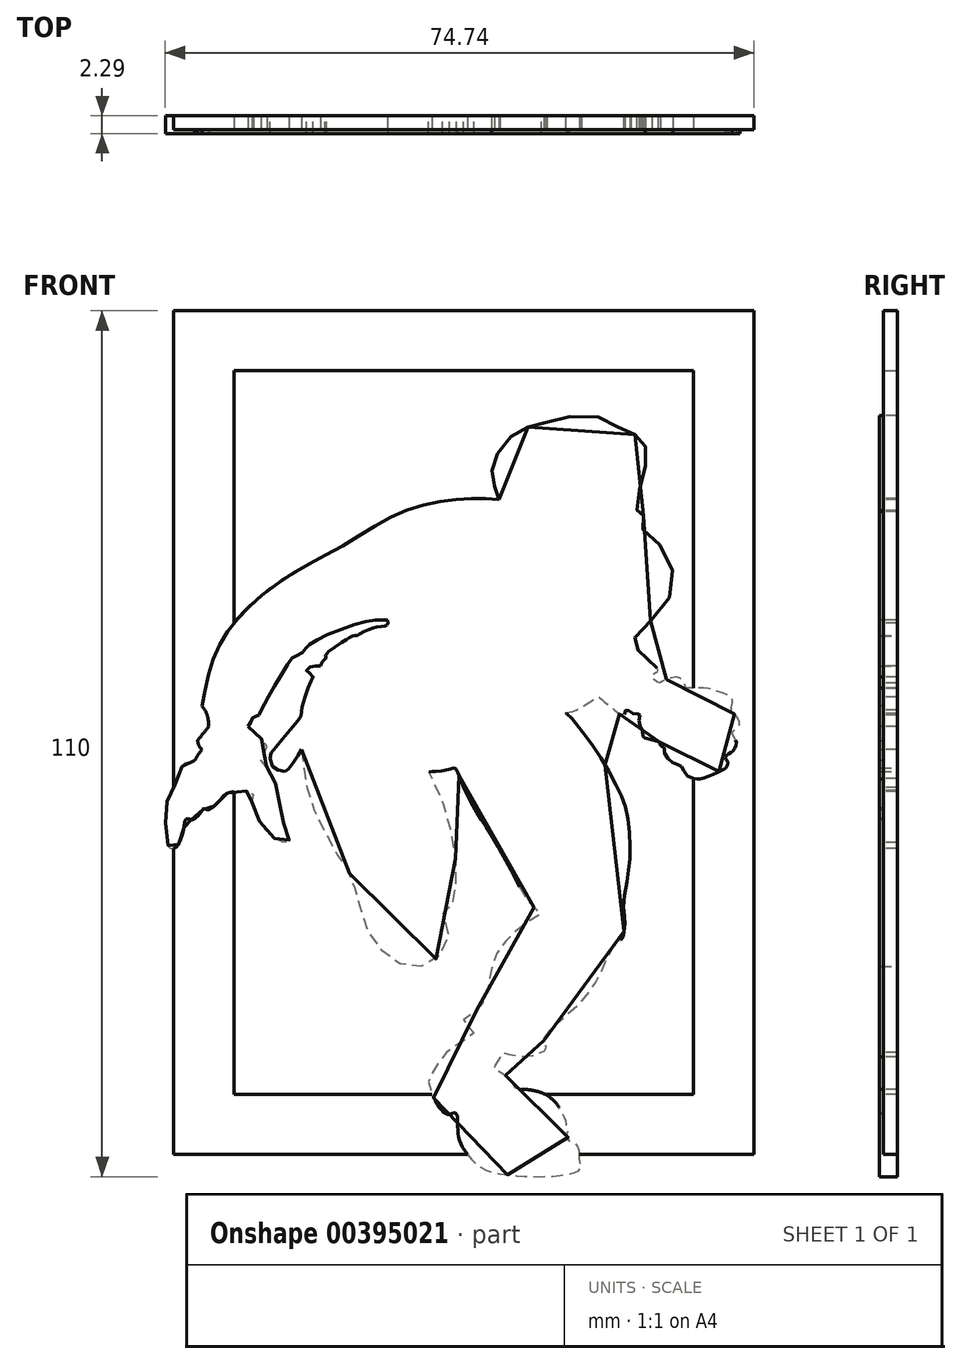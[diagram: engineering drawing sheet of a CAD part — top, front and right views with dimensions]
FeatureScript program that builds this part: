
annotation { "Feature Type Name" : "Feature", "Feature Type Description" : "" }
export const myFeature = defineFeature(function(context is Context, id is Id, definition is map)
    precondition{}
    {
        {
            var Q0;
            Q0=qCreatedBy(makeId("Front.planeOp"),FACE);
            var sketch = newSketch(context, id + "F0", { "sketchPlane" : qUnion([Q0])});
            skLineSegment(sketch, "E0", {"start": v(-44.45, 0) * mm, "end": v(44.45, 0) * mm, "construction": true});
            skLineSegment(sketch, "E1", {"start": v(0, 54.2) * mm, "end": v(0, -54.2) * mm, "construction": true});
            skPoint(sketch, "E2", {"position": v(0, 0) * mm});
            skFitSpline(sketch, "E3", {"points": [v(2.07, 37.23) * mm, v(-1.65, 37.35) * mm, v(-6.55, 36.74) * mm, v(-12, 34.82) * mm, v(-17.89, 31.29) * mm, v(-23.96, 27.94) * mm, v(-29.23, 24.04) * mm, v(-32.63, 20.14) * mm, v(-34.62, 15.8) * mm, v(-35.67, 10.97) * mm], "startDerivative": vector(-39.23, 2.67) * mm, "endDerivative": vector(-8.2, -46.44) * mm});
            skFitSpline(sketch, "E4", {"points": [v(-35.67, 10.97) * mm, v(-35.05, 9.98) * mm, v(-34.8, 8.37) * mm], "startDerivative": vector(1.56, -1.97) * mm, "endDerivative": vector(0.22, -3.2) * mm});
            skFitSpline(sketch, "E5", {"points": [v(-34.8, 8.37) * mm, v(-35.67, 7.32) * mm, v(-36.23, 6.57) * mm], "startDerivative": vector(-1.68, -2) * mm, "endDerivative": vector(-1.15, -1.58) * mm});
            skFitSpline(sketch, "E6", {"points": [v(-36.23, 6.57) * mm, v(-36.05, 5.96) * mm, v(-35.67, 5.44) * mm], "startDerivative": vector(0.24, -1.29) * mm, "endDerivative": vector(0.87, -1) * mm});
            skFitSpline(sketch, "E7", {"points": [v(-35.67, 5.44) * mm, v(-36.23, 4.68) * mm, v(-36.6, 4.04) * mm], "startDerivative": vector(-1.12, -1.44) * mm, "endDerivative": vector(-0.72, -1.34) * mm});
            skFitSpline(sketch, "E8", {"points": [v(-36.6, 4.04) * mm, v(-37.4, 3.8) * mm, v(-38.03, 3.54) * mm, v(-38.84, 1.98) * mm, v(-39.13, 0.94) * mm, v(-39.88, -0.55) * mm, v(-40.22, -1.48) * mm, v(-40.32, -3.46) * mm, v(-40.17, -5.86) * mm, v(-39.72, -7.06) * mm, v(-39.1, -7.06) * mm, v(-38.63, -6.6) * mm, v(-38.08, -4.98) * mm, v(-37.95, -4.27) * mm, v(-37.67, -3.33) * mm, v(-37.15, -3.44) * mm, v(-36.6, -3.34) * mm, v(-35.66, -2.35) * mm, v(-35.43, -1.98) * mm, v(-35, -2.19) * mm, v(-33.73, -1.33) * mm, v(-32.77, -0.24) * mm, v(-32.14, 0) * mm, v(-30.6, 0.26) * mm, v(-29.17, -0.21) * mm, v(-29.25, -0.81) * mm, v(-29.15, -1.98) * mm, v(-28.34, -3.68) * mm, v(-27.12, -5.27) * mm, v(-25.47, -6.28) * mm, v(-24.61, -6.2) * mm, v(-24.77, -5.58) * mm, v(-25.21, -4.22) * mm, v(-25.63, -2.71) * mm, v(-25.94, -0.47) * mm, v(-26.1, 0.6) * mm, v(-26.67, 2.03) * mm, v(-27.4, 3.2) * mm, v(-28.13, 4.04) * mm, v(-27.9, 4.79) * mm, v(-27.43, 5.73) * mm, v(-27.95, 6.64) * mm, v(-29.36, 8.02) * mm, v(-29.82, 8.36) * mm], "startDerivative": vector(-42.25, -13.95) * mm, "endDerivative": vector(-24.4, 15.47) * mm});
            skFitSpline(sketch, "E9", {"points": [v(-29.82, 8.36) * mm, v(-29.54, 8.76) * mm, v(-29.29, 9.4) * mm, v(-29.21, 9.55) * mm, v(-28.84, 9.64) * mm, v(-28.49, 9.78) * mm, v(-28.35, 9.97) * mm, v(-27.95, 10.85) * mm, v(-27.23, 12.18) * mm, v(-25.33, 15.4) * mm, v(-24.23, 17.07) * mm, v(-23.95, 17.26) * mm, v(-22.92, 17.77) * mm, v(-22.57, 18.23) * mm, v(-22.13, 18.67) * mm, v(-20.6, 19.63) * mm, v(-16.42, 21.28) * mm, v(-13.78, 21.93) * mm, v(-12.5, 21.91) * mm, v(-12.08, 21.88) * mm], "startDerivative": vector(8.09, 9.48) * mm, "endDerivative": vector(10.9, -0.8) * mm});
            skFitSpline(sketch, "E10", {"points": [v(-12.08, 21.88) * mm, v(-12.08, 21.42) * mm, v(-12.23, 21.22) * mm, v(-12.42, 21.16) * mm, v(-13.52, 21.03) * mm, v(-14.4, 20.72) * mm, v(-15.7, 20.12) * mm, v(-15.98, 19.92) * mm, v(-16.34, 19.95) * mm, v(-16.88, 19.73) * mm, v(-17.73, 19.19) * mm, v(-19.98, 17.47) * mm, v(-19.96, 17.24) * mm, v(-19.87, 17.15) * mm, v(-20.35, 16.62) * mm, v(-20.6, 16.12) * mm, v(-20.63, 16.05) * mm], "startDerivative": vector(1.15, -9.1) * mm, "endDerivative": vector(-1.16, -2.5) * mm});
            skFitSpline(sketch, "E11", {"points": [v(-20.63, 16.05) * mm, v(-20.99, 16.05) * mm, v(-21.48, 16.05) * mm, v(-22.06, 15.87) * mm, v(-22.4, 15.52) * mm, v(-22.39, 15.48) * mm, v(-22.29, 15.37) * mm, v(-21.85, 15.03) * mm, v(-21.56, 14.7) * mm, v(-21.68, 14.47) * mm, v(-21.92, 13.92) * mm, v(-22.39, 12.77) * mm, v(-22.93, 10.92) * mm, v(-23.13, 9.6) * mm, v(-23.22, 9.4) * mm, v(-24.7, 7.74) * mm, v(-25.96, 6.1) * mm, v(-26.86, 5.07) * mm, v(-26.94, 4.79) * mm, v(-26.97, 3.78) * mm, v(-26.3, 2.95) * mm, v(-25.67, 2.77) * mm, v(-24.86, 2.73) * mm, v(-24.73, 2.93) * mm, v(-24.23, 3.58) * mm, v(-23.42, 4.79) * mm, v(-23.02, 5.44) * mm], "startDerivative": vector(-12.7, -0.16) * mm, "endDerivative": vector(8.85, 14.94) * mm});
            skFitSpline(sketch, "E12", {"points": [v(-23.02, 5.44) * mm, v(-22.87, 4.04) * mm, v(-22.52, 1.55) * mm, v(-22.23, 0.32) * mm, v(-21.34, -2.46) * mm, v(-20.22, -4.7) * mm, v(-18.43, -7.97) * mm, v(-17.5, -9.26) * mm, v(-17.11, -9.85) * mm, v(-16.35, -11.96) * mm, v(-15.51, -14.7) * mm, v(-15.02, -16.76) * mm, v(-13.69, -19.06) * mm, v(-11.74, -21) * mm, v(-9.6, -21.97) * mm, v(-7.28, -21.9) * mm, v(-5.42, -20.6) * mm, v(-4.4, -18.72) * mm, v(-4.3, -17.26) * mm, v(-4.49, -16.98) * mm, v(-5.08, -15.84) * mm, v(-5.1, -15.53) * mm, v(-4.98, -15.28) * mm, v(-4.43, -15) * mm, v(-3.9, -14.23) * mm, v(-3.5, -12.93) * mm, v(-3.37, -10.33) * mm, v(-3.62, -6.89) * mm, v(-4.58, -2.83) * mm, v(-5.54, 0) * mm, v(-6.6, 1.91) * mm, v(-6.9, 2.5) * mm, v(-6.72, 2.65) * mm, v(-6.28, 2.65) * mm, v(-4.92, 2.78) * mm, v(-3.53, 3.12) * mm, v(-3.34, 2.93) * mm, v(-2.75, 1.48) * mm, v(-1.73, -0.82) * mm, v(-0.34, -3.2) * mm, v(1.34, -5.8) * mm, v(2.4, -7.73) * mm, v(4.47, -11.54) * mm, v(5.52, -13.49) * mm, v(6.8, -14.85) * mm, v(7.4, -15.4) * mm, v(7.4, -15.5) * mm, v(7.13, -15.6) * mm, v(5.02, -16.96) * mm, v(2.98, -18.78) * mm, v(1.46, -21.14) * mm, v(0.84, -23.86) * mm, v(0.35, -25.81) * mm, v(-0.7, -27.64) * mm, v(-2.41, -28.82) * mm, v(-2.07, -29.56) * mm, v(-1.11, -30.43) * mm, v(-1.2, -30.57) * mm, v(-1.94, -31.22) * mm, v(-3.87, -32.43) * mm, v(-5.38, -33.96) * mm, v(-6.52, -35.76) * mm, v(-6.9, -36.8) * mm, v(-6.02, -39.24) * mm, v(-4.99, -40.62) * mm, v(-4.35, -40.88) * mm, v(-3.72, -40.7) * mm, v(-3.39, -40.77) * mm, v(-3.2, -41.58) * mm, v(-3.15, -43.24) * mm, v(-2.63, -44.95) * mm, v(-1, -47.03) * mm, v(1.04, -48.18) * mm, v(5.04, -48.73) * mm, v(8.1, -48.78) * mm, v(11.42, -48.36) * mm, v(12.5, -47.63) * mm, v(12.47, -47.23) * mm, v(12.4, -47.21) * mm, v(12.32, -46.87) * mm, v(12.29, -45.97) * mm, v(12.03, -44.86) * mm, v(11.4, -44.38) * mm, v(10.93, -44.3) * mm, v(10.93, -44.18) * mm, v(10.74, -43.59) * mm, v(10.63, -43.43) * mm, v(10.8, -43.16) * mm, v(10.7, -42.78) * mm, v(10.62, -42) * mm, v(10, -40.5) * mm, v(8.68, -38.82) * mm, v(7.33, -38.1) * mm, v(5.52, -37.72) * mm, v(4.39, -37.7) * mm, v(4.17, -37.56) * mm, v(3.6, -36.65) * mm, v(2.53, -35.73) * mm, v(1.52, -35.15) * mm, v(1.57, -34.96) * mm, v(1.6, -34.73) * mm, v(2.23, -33.66) * mm, v(2.51, -33.07) * mm, v(2.6, -33.02) * mm, v(3.07, -33.16) * mm, v(4.73, -33.55) * mm, v(6.94, -33.26) * mm, v(8.1, -32.55) * mm, v(8.15, -32.4) * mm, v(8.01, -32.22) * mm, v(7.77, -32.1) * mm, v(7.77, -31.88) * mm, v(7.81, -31.26) * mm, v(9.05, -29.65) * mm, v(12.12, -26.97) * mm, v(14.04, -24.59) * mm, v(15.37, -22.05) * mm, v(16.32, -19.96) * mm, v(17.5, -18.75) * mm, v(17.87, -18.33) * mm, v(17.9, -17.85) * mm, v(18.05, -16.41) * mm, v(17.87, -14.7) * mm, v(18.4, -10.76) * mm, v(18.7, -7.41) * mm, v(18.3, -2.7) * mm, v(17.15, 0.53) * mm, v(14.3, 5.44) * mm, v(12.15, 8.36) * mm, v(10.66, 10.01) * mm, v(10.5, 10.1) * mm, v(10.6, 10.12) * mm, v(11.72, 10.45) * mm, v(14.2, 11.89) * mm, v(14.72, 12.15) * mm, v(14.84, 12.06) * mm, v(16.15, 10.99) * mm, v(17.32, 10.01) * mm, v(17.56, 9.97) * mm, v(17.76, 10.01) * mm, v(17.91, 9.86) * mm, v(18.05, 9.97) * mm, v(18.11, 10.4) * mm, v(18.25, 10.5) * mm, v(18.67, 10.27) * mm, v(19.2, 9.96) * mm, v(19.83, 10.01) * mm, v(19.97, 9.98) * mm, v(19.86, 9.65) * mm, v(19.91, 8.7) * mm, v(19.99, 8.36) * mm, v(20.42, 7.44) * mm, v(20.33, 7.02) * mm, v(20.48, 6.96) * mm, v(21.74, 6.64) * mm, v(22.54, 6.34) * mm, v(22.56, 6.17) * mm, v(22.57, 5.9) * mm, v(22.73, 5.86) * mm, v(22.98, 5.73) * mm, v(23.06, 5.6) * mm, v(23.09, 5.1) * mm, v(23.5, 4.31) * mm, v(24.15, 3.78) * mm, v(24.76, 3.55) * mm, v(25.2, 3.33) * mm, v(25.49, 2.87) * mm, v(25.97, 2.14) * mm, v(27, 1.72) * mm, v(28.18, 1.9) * mm, v(30.32, 2.8) * mm, v(30.88, 3.13) * mm, v(30.97, 3.28) * mm, v(31.1, 3.63) * mm, v(31.02, 4.04) * mm, v(30.82, 4.43) * mm, v(31.06, 4.79) * mm, v(31.73, 5.25) * mm, v(32.2, 6.06) * mm, v(32.06, 6.77) * mm, v(31.71, 7.44) * mm, v(31.73, 7.7) * mm, v(32.21, 8.15) * mm, v(32.61, 8.49) * mm, v(32.54, 9.19) * mm, v(32.09, 9.88) * mm, v(31.58, 10.38) * mm, v(31.67, 11.1) * mm, v(31.7, 11.77) * mm, v(31.44, 12.2) * mm, v(29.89, 12.81) * mm, v(28.45, 13.25) * mm, v(27.2, 13.3) * mm, v(26.03, 13.26) * mm, v(25.84, 13.26) * mm, v(25.56, 13.91) * mm, v(24.71, 14.67) * mm, v(23.97, 14.55) * mm, v(22.93, 14.22) * mm, v(22.33, 13.94) * mm, v(21.46, 14.77) * mm, v(21.5, 14.89) * mm, v(21.9, 15.2) * mm, v(22.23, 15.4) * mm, v(22.1, 15.8) * mm, v(21.58, 16.3) * mm, v(19.35, 18.5) * mm, v(18.86, 19.24) * mm, v(18.9, 19.41) * mm, v(19.4, 19.8) * mm, v(20.08, 20.7) * mm, v(22.02, 22.45) * mm, v(23.58, 24.5) * mm, v(24.15, 26.66) * mm, v(23.9, 28.92) * mm, v(22.75, 31.14) * mm, v(21.37, 32.51) * mm, v(20.38, 33.38) * mm, v(20.25, 33.57) * mm, v(20.27, 33.97) * mm, v(20.4, 35) * mm, v(20.34, 35.5) * mm, v(19.9, 35.84) * mm, v(19.52, 35.67) * mm, v(19.6, 35.95) * mm, v(19.7, 36.93) * mm, v(19.9, 38.35) * mm, v(20.44, 40.07) * mm, v(20.65, 42.1) * mm, v(20.6, 43.42) * mm, v(20.65, 43.96) * mm, v(20.3, 44.36) * mm, v(19.66, 45.28) * mm, v(19.2, 45.5) * mm, v(17.7, 46.18) * mm, v(17.26, 46.36) * mm, v(16.64, 46.89) * mm, v(15.15, 47.59) * mm, v(13, 47.88) * mm, v(10.41, 47.7) * mm, v(8.6, 47.25) * mm, v(7.2, 46.72) * mm, v(6.45, 46.52) * mm, v(5.4, 46.36) * mm, v(4.39, 45.8) * mm, v(3.55, 45.17) * mm, v(2.96, 44.46) * mm, v(1.79, 42.94) * mm, v(1.23, 41.9) * mm, v(1.17, 41.04) * mm, v(1.14, 40.47) * mm, v(1.26, 39.72) * mm, v(1.5, 38.93) * mm, v(1.9, 38.14) * mm, v(2.2, 37.37) * mm, v(2.07, 37.23) * mm], "startDerivative": vector(28.4, -278.9) * mm, "endDerivative": vector(-112.4, -58) * mm});
            skSolve(sketch);
        }
        {
            var Q0;
            Q0=qSketchRegion(id+"F0",true);
            extrude(context, id + "F1", {"entities" : qUnion([Q0]), "oppositeDirection" : true, "depth" : 2.3 * mm});
        }
        {
            var Q0;
            Q0=makeQuery(id+"F1.opExtrude","CAP_FACE",FACE,{"disambiguationData":[OSD([sQuery(id+"F0.wireOp",EDGE,"E3"),sQuery(id+"F0.wireOp",EDGE,"E4"),sQuery(id+"F0.wireOp",EDGE,"E5"),sQuery(id+"F0.wireOp",EDGE,"E6"),sQuery(id+"F0.wireOp",EDGE,"E7"),sQuery(id+"F0.wireOp",EDGE,"E8"),sQuery(id+"F0.wireOp",EDGE,"E9"),sQuery(id+"F0.wireOp",EDGE,"E10"),sQuery(id+"F0.wireOp",EDGE,"E11"),sQuery(id+"F0.wireOp",EDGE,"E12")])],"isStart":true});
            var sketch = newSketch(context, id + "F2", { "sketchPlane" : qUnion([Q0])});
            skFitSpline(sketch, "E13", {"points": [v(2.3, 37.05) * mm, v(2.58, 36.42) * mm, v(3.02, 35.55) * mm, v(3.78, 34.43) * mm, v(4.11, 33.95) * mm, v(3.9, 34.93) * mm, v(3.78, 36.33) * mm, v(3.76, 37.93) * mm, v(4.08, 40.22) * mm, v(5.22, 41.8) * mm, v(6.51, 42.35) * mm, v(8.55, 42.6) * mm, v(10.3, 41.98) * mm, v(12.03, 41.25) * mm, v(13.24, 41.14) * mm, v(15.06, 42.24) * mm, v(15.9, 42.8) * mm, v(17.03, 42.87) * mm, v(18.19, 42) * mm, v(18.91, 40.62) * mm, v(19.02, 39.55) * mm, v(19.04, 37.2) * mm, v(18.95, 34.57) * mm, v(19, 33.73) * mm, v(19.07, 34.15) * mm, v(19.36, 35.43) * mm], "startDerivative": vector(9.4, -21.56) * mm, "endDerivative": vector(8.5, 34.59) * mm});
            skFitSpline(sketch, "E14", {"points": [v(2.1, 34.71) * mm, v(2.62, 34.14) * mm, v(3, 33.38) * mm, v(3.32, 32.65) * mm], "startDerivative": vector(1.66, -1.65) * mm, "endDerivative": vector(0.92, -2.17) * mm});
            skFitSpline(sketch, "E15", {"points": [v(2.75, 35.87) * mm, v(2.36, 36.1) * mm, v(1.85, 36.13) * mm, v(1.42, 35.5) * mm, v(1.33, 34.5) * mm, v(1.77, 32.8) * mm, v(2.16, 31.91) * mm], "startDerivative": vector(-3.01, 1.98) * mm, "endDerivative": vector(2.16, -4.4) * mm});
            skFitSpline(sketch, "E16", {"points": [v(20.12, 33.4) * mm, v(19.68, 32.59) * mm, v(19.1, 31.64) * mm], "startDerivative": vector(-0.86, -1.7) * mm, "endDerivative": vector(-1.15, -1.84) * mm});
            skFitSpline(sketch, "E17", {"points": [v(18.98, 33.52) * mm, v(19.02, 31.13) * mm, v(19, 29) * mm, v(18.85, 28.03) * mm, v(17.83, 25.6) * mm, v(16.9, 24.46) * mm, v(16.28, 23.96) * mm, v(15.73, 23.27) * mm, v(13.64, 22.24) * mm, v(10.64, 22.21) * mm, v(8.36, 23.27) * mm, v(7.22, 24.24) * mm, v(6.02, 25.1) * mm, v(5.06, 26.35) * mm, v(4.5, 27.73) * mm, v(4.37, 28.62) * mm, v(4.01, 29.65) * mm], "startDerivative": vector(0.48, -30.88) * mm, "endDerivative": vector(-8.43, 20.55) * mm});
            skCircle(sketch, "E18", {"center": v(2.83, 30.82) * mm, "radius": 1.11 * mm});
            skFitSpline(sketch, "E19", {"points": [v(11.33, 29.52) * mm, v(12.1, 29.5) * mm, v(12.71, 29.21) * mm, v(13.35, 29) * mm, v(14.18, 29.32) * mm, v(15, 29.8) * mm, v(15.54, 29.87) * mm], "startDerivative": vector(4.72, 0.3) * mm, "endDerivative": vector(3.72, -0.03) * mm});
            skFitSpline(sketch, "E20", {"points": [v(8, 27.33) * mm, v(7.78, 26.98) * mm, v(7.76, 26.5) * mm, v(7.94, 26.32) * mm], "startDerivative": vector(-0.72, -0.88) * mm, "endDerivative": vector(0.77, -0.49) * mm});
            skFitSpline(sketch, "E21", {"points": [v(9.51, 26.98) * mm, v(10.68, 27.5) * mm, v(11.66, 27.88) * mm, v(13.1, 27.88) * mm, v(13.76, 27.84) * mm, v(14.7, 28.12) * mm, v(15.67, 28.01) * mm, v(16.44, 27.46) * mm], "startDerivative": vector(7.64, 3.36) * mm, "endDerivative": vector(5.28, -4.62) * mm});
            skFitSpline(sketch, "E22", {"points": [v(17.64, 27.4) * mm, v(17.36, 27.6) * mm, v(17.03, 27.64) * mm, v(16.61, 27.35) * mm, v(16.13, 27.07) * mm, v(14.84, 26.65) * mm, v(13.87, 26.2) * mm, v(13.52, 25.93) * mm, v(13.22, 25.9) * mm, v(12.54, 26.13) * mm, v(11.49, 26.46) * mm, v(10.68, 26.5) * mm, v(9.51, 26.46) * mm, v(9.01, 26.48) * mm, v(8.84, 26.65) * mm], "startDerivative": vector(-5.14, 4.15) * mm, "endDerivative": vector(-3.27, 4.66) * mm});
            skFitSpline(sketch, "E23", {"points": [v(9.8, 25.5) * mm, v(10.48, 24.86) * mm, v(11.55, 24.09) * mm, v(12.73, 23.98) * mm, v(14.55, 24.44) * mm, v(15.34, 25.18) * mm, v(15.65, 25.73) * mm, v(15.73, 26.24) * mm], "startDerivative": vector(4.64, -4.44) * mm, "endDerivative": vector(0.49, 5.08) * mm});
            skFitSpline(sketch, "E24", {"points": [v(7.18, 35.08) * mm, v(8.25, 35.2) * mm, v(9.68, 34.96) * mm, v(10.6, 34.45) * mm, v(11.1, 34.03) * mm, v(11.78, 34.17) * mm, v(12.24, 34.85) * mm], "startDerivative": vector(5.68, 1.09) * mm, "endDerivative": vector(2.35, 5) * mm});
            skFitSpline(sketch, "E25", {"points": [v(8.43, 36.51) * mm, v(9.37, 36.5) * mm, v(9.88, 36.07) * mm, v(10.6, 35.3) * mm, v(11.06, 34.32) * mm], "startDerivative": vector(4.14, 0.43) * mm, "endDerivative": vector(1.4, -3.78) * mm});
            skFitSpline(sketch, "E26", {"points": [v(7.45, 34.93) * mm, v(7.79, 34.48) * mm, v(8.1, 34.15) * mm, v(8.5, 33.81) * mm], "startDerivative": vector(0.99, -1.35) * mm, "endDerivative": vector(1.29, -1) * mm});
            skFitSpline(sketch, "E27", {"points": [v(9.2, 34.93) * mm, v(9.17, 34.51) * mm, v(9.3, 34.06) * mm, v(9.63, 33.96) * mm, v(9.99, 34.07) * mm, v(10.2, 34.38) * mm, v(10.26, 34.6) * mm], "startDerivative": vector(-0.42, -2.2) * mm, "endDerivative": vector(0.26, 1.57) * mm});
            skFitSpline(sketch, "E28", {"points": [v(14.93, 34.15) * mm, v(15.66, 35) * mm, v(16.27, 35.94) * mm, v(16.71, 36.89) * mm], "startDerivative": vector(2.23, 2.47) * mm, "endDerivative": vector(1.24, 2.95) * mm});
            skFitSpline(sketch, "E29", {"points": [v(15.66, 34.68) * mm, v(15.81, 34.22) * mm, v(16.1, 33.98) * mm, v(16.46, 34.14) * mm, v(16.66, 34.56) * mm, v(16.67, 35.15) * mm], "startDerivative": vector(0.53, -2.35) * mm, "endDerivative": vector(-0.14, 2.7) * mm});
            skFitSpline(sketch, "E30", {"points": [v(16, 35.21) * mm, v(16.55, 35.33) * mm, v(17.23, 35.29) * mm, v(17.78, 35.41) * mm, v(18.39, 35.82) * mm], "startDerivative": vector(2.2, 0.72) * mm, "endDerivative": vector(2.24, 1.73) * mm});
            skFitSpline(sketch, "E31", {"points": [v(17.64, 35.26) * mm, v(17.6, 34.85) * mm, v(17.35, 34.48) * mm, v(17.05, 34.12) * mm], "startDerivative": vector(0.02, -1.3) * mm, "endDerivative": vector(-0.85, -1.05) * mm});
            skFitSpline(sketch, "E32", {"points": [v(2.55, 38.25) * mm, v(2.17, 41.02) * mm, v(2.94, 42.4) * mm, v(4.56, 43.73) * mm, v(5.23, 43.95) * mm, v(4.02, 44.05) * mm, v(4.88, 44.67) * mm, v(7.66, 45.86) * mm], "startDerivative": vector(-4.09, 16.61) * mm, "endDerivative": vector(14.9, 6.03) * mm});
            skSolve(sketch);
        }
        {
            var Q0;
            Q0=qSketchRegion(id+"F2",true);
            var Q1;
            Q1=sQuery(id+"F2.wireOp",EDGE,"d9569821-eecf-49fa-9423-2ff2d1b1941c");
            var Q2;
            Q2=sQuery(id+"F2.wireOp",EDGE,"7pOSf9LI-wKQY-qpFU-wMJt-ItYx99x1vwxx");
            var Q3;
            Q3=sQuery(id+"F2.wireOp",EDGE,"vgNLgwYX-bfzJ-7AqC-6rUm-0AJOgbjPAZjm");
            var Q4;
            Q4=sQuery(id+"F2.wireOp",EDGE,"1a1bac1e-a555-4706-be7b-ffc530e547ce");
            var Q5;
            Q5=sQuery(id+"F2.wireOp",EDGE,"E13");
            var Q6;
            Q6=sQuery(id+"F2.wireOp",EDGE,"E16");
            var Q7;
            Q7=sQuery(id+"F2.wireOp",EDGE,"E17");
            var Q8;
            Q8=sQuery(id+"F2.wireOp",EDGE,"E18");
            var Q9;
            Q9=sQuery(id+"F2.wireOp",EDGE,"E15");
            var Q10;
            Q10=sQuery(id+"F2.wireOp",EDGE,"E14");
            var Q11;
            Q11=sQuery(id+"F2.wireOp",EDGE,"E19");
            var Q12;
            Q12=sQuery(id+"F2.wireOp",EDGE,"E21");
            var Q13;
            Q13=sQuery(id+"F2.wireOp",EDGE,"E20");
            var Q14;
            Q14=sQuery(id+"F2.wireOp",EDGE,"E23");
            var Q15;
            Q15=sQuery(id+"F2.wireOp",EDGE,"E22");
            var Q16;
            Q16=sQuery(id+"F2.wireOp",EDGE,"E26");
            var Q17;
            Q17=sQuery(id+"F2.wireOp",EDGE,"E24");
            var Q18;
            Q18=sQuery(id+"F2.wireOp",EDGE,"E27");
            var Q19;
            Q19=sQuery(id+"F2.wireOp",EDGE,"E25");
            var Q20;
            Q20=sQuery(id+"F2.wireOp",EDGE,"E28");
            var Q21;
            Q21=sQuery(id+"F2.wireOp",EDGE,"E29");
            var Q22;
            Q22=sQuery(id+"F2.wireOp",EDGE,"E30");
            var Q23;
            Q23=sQuery(id+"F2.wireOp",EDGE,"E31");
            var Q24;
            Q24=sQuery(id+"F2.wireOp",EDGE,"1e27200c-010a-4161-a363-a86046994168");
            var Q25;
            Q25=sQuery(id+"F2.wireOp",EDGE,"E32");
            extrude(context, id + "F3", {"entities" : qUnion([Q0]), "bodyType" : ToolBodyType.SURFACE, "surfaceEntities" : qUnion([Q1, Q2, Q3, Q4, Q5, Q6, Q7, Q8, Q9, Q10, Q11, Q12, Q13, Q14, Q15, Q16, Q17, Q18, Q19, Q20, Q21, Q22, Q23, Q24, Q25]), "depth" : 0.13 * mm});
        }
        {
            var Q0;
            Q0=makeQuery(id+"F0.imprint","IMPRINT",FACE,{"disambiguationData":[TD([[makeQuery(id+"F0.imprint","IMPRINT",EDGE,{"derivedFrom":sQuery(id+"F0.wireOp",EDGE,"E3")}),1.0]])]});
            var sketch = newSketch(context, id + "F4", { "sketchPlane" : qUnion([Q0])});
            skFitSpline(sketch, "E33", {"points": [v(-34.82, 10.54) * mm, v(-33.64, 11.76) * mm, v(-31.38, 12.43) * mm, v(-29.38, 10.8) * mm, v(-29.08, 9.98) * mm], "startDerivative": vector(4.16, 5.18) * mm, "endDerivative": vector(0.82, -4.17) * mm});
            skFitSpline(sketch, "E34", {"points": [v(-34.6, 8.06) * mm, v(-33.41, 8.58) * mm, v(-31.52, 8.72) * mm, v(-30.2, 8.4) * mm], "startDerivative": vector(3.49, 1.9) * mm, "endDerivative": vector(3.9, -1.32) * mm});
            skFitSpline(sketch, "E35", {"points": [v(-38.27, -3.9) * mm, v(-38.56, -4.35) * mm, v(-38.82, -4.43) * mm, v(-39.12, -3.32) * mm, v(-39.05, -0.54) * mm, v(-38.9, 0.54) * mm], "startDerivative": vector(-1.85, -3.5) * mm, "endDerivative": vector(0.74, 4.42) * mm});
            skFitSpline(sketch, "E36", {"points": [v(-36.71, 3.5) * mm, v(-37.23, 1.39) * mm, v(-37.71, -1.2) * mm, v(-37.75, -2.58) * mm, v(-37.53, -3.06) * mm], "startDerivative": vector(-1.76, -6.84) * mm, "endDerivative": vector(1.81, -2.9) * mm});
            skFitSpline(sketch, "E37", {"points": [v(-35.27, 5.61) * mm, v(-34.45, 5.8) * mm, v(-33.55, 5.48) * mm], "startDerivative": vector(1.67, 0.63) * mm, "endDerivative": vector(1.76, -0.88) * mm});
            skFitSpline(sketch, "E38", {"points": [v(-32.49, 0.54) * mm, v(-31.45, 2.06) * mm, v(-30.57, 3.39) * mm], "startDerivative": vector(2.05, 2.98) * mm, "endDerivative": vector(1.78, 2.72) * mm});
            skFitSpline(sketch, "E39", {"points": [v(-11.38, 22.24) * mm, v(-8.94, 22.87) * mm, v(-5.3, 23.79) * mm], "startDerivative": vector(5.14, 1.34) * mm, "endDerivative": vector(6.95, 1.74) * mm});
            skFitSpline(sketch, "E40", {"points": [v(-9.47, 22.42) * mm, v(-6.72, 22.27) * mm], "startDerivative": vector(2.75, -0.16) * mm, "endDerivative": vector(2.75, -0.16) * mm});
            skFitSpline(sketch, "E41", {"points": [v(-8.55, 23.34) * mm, v(-7.71, 25.18) * mm, v(-7.3, 28.27) * mm, v(-7.4, 30.91) * mm, v(-8.05, 33.24) * mm, v(-8.92, 34.84) * mm], "startDerivative": vector(5.1, 9.05) * mm, "endDerivative": vector(-5.22, 8.58) * mm});
            skFitSpline(sketch, "E42", {"points": [v(-12.06, 21.1) * mm, v(-12.09, 18.69) * mm, v(-11.44, 15.88) * mm, v(-10.6, 12.98) * mm, v(-10.12, 12.35) * mm, v(-8.6, 10.22) * mm, v(-7.19, 8.89) * mm, v(-6.7, 8.56) * mm, v(-6.45, 8.59) * mm, v(-5.2, 9.56) * mm, v(-3.14, 10.36) * mm, v(-0.44, 12.11) * mm, v(1.93, 14.5) * mm, v(3.32, 17.23) * mm, v(4.17, 20.44) * mm, v(4.05, 20.61) * mm, v(3.17, 21.15) * mm, v(1.59, 23.04) * mm, v(0.66, 25.07) * mm, v(-0.5, 27.74) * mm, v(-1.08, 30.66) * mm, v(-0.87, 33.24) * mm, v(0.78, 37.02) * mm], "startDerivative": vector(-3.53, -49.44) * mm, "endDerivative": vector(31.25, 61.75) * mm});
            skFitSpline(sketch, "E43", {"points": [v(-4.72, 19.77) * mm, v(-3.58, 19.4) * mm, v(-2.8, 19.09) * mm, v(-2.8, 19) * mm, v(-3.32, 18.26) * mm, v(-4.54, 16.65) * mm, v(-4.4, 16.64) * mm, v(-3.84, 16.57) * mm, v(-2.53, 16.5) * mm, v(-2.43, 16.6) * mm, v(-1.68, 17.82) * mm, v(-1.01, 18.8) * mm, v(-0.87, 18.8) * mm, v(-0.23, 18.72) * mm, v(0.78, 18.54) * mm, v(0.91, 18.58) * mm, v(1.33, 19.13) * mm, v(1.5, 19.5) * mm, v(1.4, 19.67) * mm, v(0.78, 19.98) * mm, v(-0.58, 20.3) * mm, v(-2.7, 20.28) * mm, v(-4.16, 20.06) * mm, v(-4.72, 19.77) * mm]});
            skFitSpline(sketch, "E44", {"points": [v(11.75, 21.87) * mm, v(12.2, 20.12) * mm, v(11.67, 17.08) * mm, v(10.55, 14.38) * mm, v(8.37, 11.53) * mm, v(5.83, 9.3) * mm, v(5.15, 8.4) * mm, v(5.41, 8.4) * mm, v(6.38, 8.9) * mm, v(9, 9.98) * mm, v(9.97, 9.98) * mm], "startDerivative": vector(6.4, -16.53) * mm, "endDerivative": vector(11.48, -1.85) * mm});
            skFitSpline(sketch, "E45", {"points": [v(15.08, 12.76) * mm, v(16.05, 13.75) * mm, v(17.25, 15.9) * mm, v(17.88, 17.94) * mm, v(18.56, 18.78) * mm], "startDerivative": vector(4.25, 3.86) * mm, "endDerivative": vector(3.8, 3.57) * mm});
            skFitSpline(sketch, "E46", {"points": [v(18.17, 11.05) * mm, v(18.59, 12.47) * mm, v(20.53, 14.33) * mm, v(21.13, 14.62) * mm], "startDerivative": vector(0.41, 4.08) * mm, "endDerivative": vector(2.24, 0.77) * mm});
            skFitSpline(sketch, "E47", {"points": [v(20.13, 10.22) * mm, v(20.72, 11.37) * mm, v(21.33, 12.58) * mm, v(22.22, 13.69) * mm], "startDerivative": vector(1.87, 3.48) * mm, "endDerivative": vector(2.8, 3.15) * mm});
            skFitSpline(sketch, "E48", {"points": [v(23.28, 6.32) * mm, v(23.22, 7.43) * mm, v(22.66, 8.2) * mm, v(22.2, 9.56) * mm, v(22.28, 10.52) * mm, v(23, 11.78) * mm], "startDerivative": vector(0.51, 6.23) * mm, "endDerivative": vector(3.93, 5.87) * mm});
            skFitSpline(sketch, "E49", {"points": [v(25.52, 10.9) * mm, v(26.76, 10.22) * mm, v(27.54, 8.8) * mm, v(27.57, 8.1) * mm, v(27.63, 7.7) * mm, v(27.46, 6.9) * mm, v(27.35, 5.93) * mm, v(27.37, 5.62) * mm, v(26.46, 4.69) * mm, v(25.17, 4.93) * mm, v(24.81, 5.85) * mm, v(24.72, 6.9) * mm, v(24.4, 7.35) * mm, v(23.7, 7.6) * mm, v(23.33, 7.7) * mm], "startDerivative": vector(14.33, -5.15) * mm, "endDerivative": vector(-6.79, 2.2) * mm});
            skFitSpline(sketch, "E50", {"points": [v(25.64, 13.02) * mm, v(25.39, 12.83) * mm, v(24.4, 12.5) * mm], "startDerivative": vector(-0.58, -0.52) * mm, "endDerivative": vector(-1.78, -0.52) * mm});
            skFitSpline(sketch, "E51", {"points": [v(-30.16, 5.28) * mm, v(-31.1, 6.38) * mm, v(-31.45, 6.8) * mm, v(-32.35, 6.78) * mm, v(-32.94, 6) * mm, v(-33.9, 4.27) * mm, v(-34.5, 2.74) * mm, v(-35.06, -0.31) * mm, v(-35.26, -1.65) * mm], "startDerivative": vector(-8.67, 9.5) * mm, "endDerivative": vector(-1.37, -9.36) * mm});
            skFitSpline(sketch, "E52", {"points": [v(26.8, 11.57) * mm, v(26.96, 10.83) * mm, v(27.02, 10.22) * mm], "startDerivative": vector(0.34, -1.44) * mm, "endDerivative": vector(0.1, -1.24) * mm});
            skFitSpline(sketch, "E53", {"points": [v(27.39, 10.22) * mm, v(28.17, 10.78) * mm, v(28.89, 11.4) * mm], "startDerivative": vector(1.6, 1.06) * mm, "endDerivative": vector(1.4, 1.28) * mm});
            skFitSpline(sketch, "E54", {"points": [v(27.93, 7.82) * mm, v(28.35, 7.76) * mm, v(28.9, 8.15) * mm, v(30.61, 9.49) * mm, v(31.3, 10.22) * mm], "startDerivative": vector(2.65, -0.8) * mm, "endDerivative": vector(2.15, 2.66) * mm});
            skFitSpline(sketch, "E55", {"points": [v(27.62, 5.45) * mm, v(28.45, 5.54) * mm, v(29.7, 6.47) * mm, v(31.41, 7.52) * mm], "startDerivative": vector(3.2, -0.17) * mm, "endDerivative": vector(4.5, 2.46) * mm});
            skFitSpline(sketch, "E56", {"points": [v(26.55, 4.3) * mm, v(27.42, 3.68) * mm, v(29.28, 3.7) * mm, v(30.5, 4.5) * mm], "startDerivative": vector(2.53, -2.55) * mm, "endDerivative": vector(3.2, 2.8) * mm});
            skFitSpline(sketch, "E57", {"points": [v(-16.05, 19.52) * mm, v(-16.2, 17.97) * mm, v(-16.08, 16.77) * mm, v(-15.42, 15.25) * mm, v(-14.43, 13.9) * mm, v(-13.04, 12.42) * mm, v(-12.2, 11.7) * mm, v(-12, 11.63) * mm, v(-11.6, 11.57) * mm, v(-10.81, 11.23) * mm, v(-9.66, 10.56) * mm, v(-8.85, 10.17) * mm], "startDerivative": vector(-1.83, -14.94) * mm, "endDerivative": vector(9.33, -4.23) * mm});
            skFitSpline(sketch, "E58", {"points": [v(-21.33, 14.6) * mm, v(-20.07, 13.34) * mm, v(-18.81, 11.73) * mm, v(-18.48, 11.2) * mm, v(-18.45, 10.73) * mm, v(-18.39, 10.22) * mm, v(-18.09, 9.8) * mm, v(-17.5, 9.44) * mm, v(-17.06, 9.34) * mm, v(-16.22, 9.57) * mm, v(-15.36, 10.47) * mm, v(-15.09, 11.26) * mm, v(-15.15, 12.04) * mm, v(-15.52, 12.72) * mm, v(-16.2, 12.93) * mm, v(-16.94, 12.99) * mm, v(-17.28, 13.24) * mm, v(-17.9, 13.92) * mm, v(-18.93, 14.96) * mm, v(-20.26, 15.72) * mm, v(-20.62, 15.84) * mm], "startDerivative": vector(17.03, -15.74) * mm, "endDerivative": vector(-8.74, 2.39) * mm});
            skFitSpline(sketch, "E59", {"points": [v(-17.47, 12.55) * mm, v(-18.05, 11.99) * mm, v(-18.3, 11.41) * mm], "startDerivative": vector(-1.24, -1.02) * mm, "endDerivative": vector(-0.4, -1.26) * mm});
            skFitSpline(sketch, "E60", {"points": [v(-15.38, 11.73) * mm, v(-15.75, 12.04) * mm, v(-16.78, 11.73) * mm, v(-17.44, 10.93) * mm, v(-17.6, 10.22) * mm], "startDerivative": vector(-1.53, 2.07) * mm, "endDerivative": vector(-0.4, -2.96) * mm});
            skFitSpline(sketch, "E61", {"points": [v(-15.88, 9.41) * mm, v(-14.75, 8.52) * mm, v(-13.57, 7.94) * mm, v(-11.87, 6.87) * mm, v(-10.88, 6.56) * mm, v(-9.7, 6.5) * mm, v(-8.6, 6.23) * mm, v(-6.59, 5.9) * mm, v(-6.28, 5.78) * mm, v(-6.2, 5.36) * mm, v(-5.77, 5.15) * mm, v(-3.6, 5.13) * mm, v(-1.9, 5.32) * mm, v(-1.12, 5.44) * mm, v(-0.9, 5.6) * mm, v(-0.8, 5.9) * mm, v(0.2, 6.08) * mm, v(2.48, 6.84) * mm, v(5.02, 8.17) * mm], "startDerivative": vector(17.97, -16.04) * mm, "endDerivative": vector(28.82, 15.95) * mm});
            skFitSpline(sketch, "E62", {"points": [v(6.21, 10.22) * mm, v(4.45, 9.57) * mm, v(2.58, 8.88) * mm, v(0.94, 8.4) * mm, v(-0.26, 8.4) * mm, v(-0.62, 8.4) * mm, v(-1.1, 8.66) * mm, v(-2.42, 8.82) * mm, v(-4.16, 8.76) * mm, v(-5.92, 8.8) * mm], "startDerivative": vector(-13.12, -4.87) * mm, "endDerivative": vector(-13.7, 0.5) * mm});
            skFitSpline(sketch, "E63", {"points": [v(2.86, 8.79) * mm, v(2.98, 7.32) * mm], "startDerivative": vector(0.12, -1.47) * mm, "endDerivative": vector(0.12, -1.47) * mm});
            skFitSpline(sketch, "E64", {"points": [v(-0.42, 8.07) * mm, v(-0.53, 6.87) * mm, v(-0.7, 6.34) * mm], "startDerivative": vector(-0.12, -2.22) * mm, "endDerivative": vector(-0.49, -1.16) * mm});
            skFitSpline(sketch, "E65", {"points": [v(-3.35, 7.7) * mm, v(-4.2, 7.4) * mm, v(-4.52, 6.9) * mm, v(-4.18, 6.36) * mm, v(-3.45, 6.28) * mm, v(-2.37, 6.46) * mm, v(-1.8, 6.72) * mm, v(-1.63, 7.23) * mm, v(-1.65, 7.43) * mm], "startDerivative": vector(-6.34, -1.4) * mm, "endDerivative": vector(-0.43, 2.42) * mm});
            skFitSpline(sketch, "E66", {"points": [v(-5.06, 8.4) * mm, v(-5.47, 7.61) * mm, v(-6.22, 6.14) * mm], "startDerivative": vector(-0.92, -1.7) * mm, "endDerivative": vector(-1.38, -2.76) * mm});
            skFitSpline(sketch, "E67", {"points": [v(-8.31, 9.04) * mm, v(-9.03, 7.75) * mm, v(-9.52, 6.8) * mm], "startDerivative": vector(-1.4, -2.49) * mm, "endDerivative": vector(-0.99, -1.99) * mm});
            skFitSpline(sketch, "E68", {"points": [v(-12.24, 11.2) * mm, v(-13.33, 9.57) * mm, v(-14.06, 8.64) * mm], "startDerivative": vector(-2, -3.1) * mm, "endDerivative": vector(-1.61, -1.96) * mm});
            skFitSpline(sketch, "E69", {"points": [v(-3.04, 3.53) * mm, v(-0.83, 4.13) * mm, v(0.9, 4.48) * mm, v(4, 4.77) * mm], "startDerivative": vector(7.05, 1.99) * mm, "endDerivative": vector(8.79, 0.69) * mm});
            skFitSpline(sketch, "E70", {"points": [v(-15.44, -11.26) * mm, v(-14.24, -15.37) * mm, v(-11.98, -18.9) * mm, v(-10.65, -20.3) * mm, v(-8.6, -21.2) * mm, v(-7.6, -21.15) * mm], "startDerivative": vector(3.29, -16.02) * mm, "endDerivative": vector(7.15, 1.32) * mm});
            skFitSpline(sketch, "E71", {"points": [v(-16.22, -10.01) * mm, v(-13.86, -11.98) * mm, v(-10.27, -14.5) * mm, v(-7.5, -15.46) * mm, v(-5.47, -15.4) * mm], "startDerivative": vector(8.76, -7.44) * mm, "endDerivative": vector(9.7, 1.04) * mm});
            skFitSpline(sketch, "E72", {"points": [v(7.75, -15.53) * mm, v(9.34, -16.85) * mm], "startDerivative": vector(1.59, -1.32) * mm, "endDerivative": vector(1.59, -1.32) * mm});
            skFitSpline(sketch, "E73", {"points": [v(-0.72, -30.65) * mm, v(1.03, -31.88) * mm, v(2.36, -32.66) * mm], "startDerivative": vector(3.33, -2.42) * mm, "endDerivative": vector(2.8, -1.57) * mm});
            skFitSpline(sketch, "E74", {"points": [v(-0.99, -31.11) * mm, v(-3.06, -32.68) * mm, v(-4.63, -33.97) * mm, v(-5.47, -35.9) * mm, v(-6.15, -37.62) * mm], "startDerivative": vector(-7.63, -5.97) * mm, "endDerivative": vector(-3, -7.12) * mm});
            skFitSpline(sketch, "E75", {"points": [v(1.69, -32.93) * mm, v(0.85, -34.17) * mm, v(-0.72, -34.1) * mm], "startDerivative": vector(-1.34, -3.16) * mm, "endDerivative": vector(-3.45, 0.79) * mm});
            skFitSpline(sketch, "E76", {"points": [v(0.8, -34.51) * mm, v(1.14, -35.68) * mm, v(2.33, -36.62) * mm, v(3.11, -37.64) * mm, v(3.45, -38.59) * mm], "startDerivative": vector(0.53, -5.13) * mm, "endDerivative": vector(1.26, -4.21) * mm});
            skFitSpline(sketch, "E77", {"points": [v(1.79, -40.13) * mm, v(3.06, -39.08) * mm, v(6.16, -38.7) * mm, v(8.44, -39.9) * mm, v(9.34, -42.1) * mm, v(10.14, -45.06) * mm], "startDerivative": vector(6.42, 7.16) * mm, "endDerivative": vector(3.75, -13.8) * mm});
            skFitSpline(sketch, "E78", {"points": [v(7.35, -46.1) * mm, v(9.42, -45.68) * mm, v(10.47, -45.29) * mm, v(11.01, -45.17) * mm, v(11.12, -45.68) * mm, v(11.33, -46.72) * mm], "startDerivative": vector(7.72, 1.38) * mm, "endDerivative": vector(1.34, -5.2) * mm});
            skFitSpline(sketch, "E79", {"points": [v(-22.87, 9.57) * mm, v(-21.9, 10.67) * mm, v(-20.9, 11.73) * mm, v(-20.34, 12.37) * mm, v(-20.27, 12.19) * mm, v(-20.08, 11.59) * mm, v(-19.67, 11.2) * mm, v(-19.16, 10.91) * mm, v(-19.42, 10.65) * mm, v(-20.5, 9.41) * mm, v(-22.1, 7.1) * mm, v(-22.79, 5.73) * mm], "startDerivative": vector(8.54, 10.16) * mm, "endDerivative": vector(-5.04, -11.13) * mm});
            skFitSpline(sketch, "E80", {"points": [v(-20.28, 12.62) * mm, v(-20.17, 12.86) * mm, v(-19.78, 12.59) * mm, v(-19.4, 11.99) * mm, v(-18.81, 11.38) * mm, v(-18.81, 11.2) * mm, v(-19.06, 11.08) * mm], "startDerivative": vector(0.53, 2.5) * mm, "endDerivative": vector(-2.22, -0.66) * mm});
            skFitSpline(sketch, "E81", {"points": [v(3.94, 18.22) * mm, v(5.37, 17.57) * mm, v(8.59, 17.57) * mm, v(10.74, 18) * mm, v(11.62, 18.7) * mm, v(11.9, 18.96) * mm], "startDerivative": vector(6.1, -3.87) * mm, "endDerivative": vector(2.35, 2.31) * mm});
            skFitSpline(sketch, "E82", {"points": [v(-19.78, 16.97) * mm, v(-19.6, 16.16) * mm, v(-19.35, 15.41) * mm], "startDerivative": vector(-0.08, -1.76) * mm, "endDerivative": vector(0.48, -2.15) * mm});
            skSolve(sketch);
        }
        {
            var Q0;
            Q0=qSketchRegion(id+"F4",true);
            var Q1;
            Q1=sQuery(id+"F4.wireOp",EDGE,"E33");
            var Q2;
            Q2=sQuery(id+"F4.wireOp",EDGE,"E35");
            var Q3;
            Q3=sQuery(id+"F4.wireOp",EDGE,"E36");
            var Q4;
            Q4=sQuery(id+"F4.wireOp",EDGE,"E37");
            var Q5;
            Q5=sQuery(id+"F4.wireOp",EDGE,"E34");
            var Q6;
            Q6=sQuery(id+"F4.wireOp",EDGE,"E51");
            var Q7;
            Q7=sQuery(id+"F4.wireOp",EDGE,"E38");
            var Q8;
            Q8=sQuery(id+"F4.wireOp",EDGE,"E42");
            var Q9;
            Q9=sQuery(id+"F4.wireOp",EDGE,"E41");
            var Q10;
            Q10=sQuery(id+"F4.wireOp",EDGE,"E39");
            var Q11;
            Q11=sQuery(id+"F4.wireOp",EDGE,"E40");
            var Q12;
            Q12=sQuery(id+"F4.wireOp",EDGE,"E43");
            var Q13;
            Q13=sQuery(id+"F4.wireOp",EDGE,"E44");
            var Q14;
            Q14=sQuery(id+"F4.wireOp",EDGE,"E45");
            var Q15;
            Q15=sQuery(id+"F4.wireOp",EDGE,"E46");
            var Q16;
            Q16=sQuery(id+"F4.wireOp",EDGE,"E47");
            var Q17;
            Q17=sQuery(id+"F4.wireOp",EDGE,"E48");
            var Q18;
            Q18=sQuery(id+"F4.wireOp",EDGE,"E50");
            var Q19;
            Q19=sQuery(id+"F4.wireOp",EDGE,"E49");
            var Q20;
            Q20=sQuery(id+"F4.wireOp",EDGE,"E56");
            var Q21;
            Q21=sQuery(id+"F4.wireOp",EDGE,"E55");
            var Q22;
            Q22=sQuery(id+"F4.wireOp",EDGE,"E54");
            var Q23;
            Q23=sQuery(id+"F4.wireOp",EDGE,"E53");
            var Q24;
            Q24=sQuery(id+"F4.wireOp",EDGE,"E52");
            var Q25;
            Q25=sQuery(id+"F4.wireOp",EDGE,"E79");
            var Q26;
            Q26=sQuery(id+"F4.wireOp",EDGE,"E80");
            var Q27;
            Q27=sQuery(id+"F4.wireOp",EDGE,"E58");
            var Q28;
            Q28=sQuery(id+"F4.wireOp",EDGE,"E59");
            var Q29;
            Q29=sQuery(id+"F4.wireOp",EDGE,"E60");
            var Q30;
            Q30=sQuery(id+"F4.wireOp",EDGE,"E57");
            var Q31;
            Q31=sQuery(id+"F4.wireOp",EDGE,"E68");
            var Q32;
            Q32=sQuery(id+"F4.wireOp",EDGE,"E61");
            var Q33;
            Q33=sQuery(id+"F4.wireOp",EDGE,"E67");
            var Q34;
            Q34=sQuery(id+"F4.wireOp",EDGE,"E66");
            var Q35;
            Q35=sQuery(id+"F4.wireOp",EDGE,"E65");
            var Q36;
            Q36=sQuery(id+"F4.wireOp",EDGE,"E62");
            var Q37;
            Q37=sQuery(id+"F4.wireOp",EDGE,"E64");
            var Q38;
            Q38=sQuery(id+"F4.wireOp",EDGE,"E63");
            var Q39;
            Q39=sQuery(id+"F4.wireOp",EDGE,"E69");
            var Q40;
            Q40=sQuery(id+"F4.wireOp",EDGE,"E71");
            var Q41;
            Q41=sQuery(id+"F4.wireOp",EDGE,"E70");
            var Q42;
            Q42=sQuery(id+"F4.wireOp",EDGE,"E72");
            var Q43;
            Q43=sQuery(id+"F4.wireOp",EDGE,"E74");
            var Q44;
            Q44=sQuery(id+"F4.wireOp",EDGE,"E73");
            var Q45;
            Q45=sQuery(id+"F4.wireOp",EDGE,"E75");
            var Q46;
            Q46=sQuery(id+"F4.wireOp",EDGE,"E76");
            var Q47;
            Q47=sQuery(id+"F4.wireOp",EDGE,"E77");
            var Q48;
            Q48=sQuery(id+"F4.wireOp",EDGE,"E78");
            var Q49;
            Q49=sQuery(id+"F4.wireOp",EDGE,"E81");
            var Q50;
            Q50=sQuery(id+"F4.wireOp",EDGE,"E82");
            extrude(context, id + "F5", {"entities" : qUnion([Q0]), "bodyType" : ToolBodyType.SURFACE, "operationType" : NewBodyOperationType.ADD, "surfaceEntities" : qUnion([Q1, Q2, Q3, Q4, Q5, Q6, Q7, Q8, Q9, Q10, Q11, Q12, Q13, Q14, Q15, Q16, Q17, Q18, Q19, Q20, Q21, Q22, Q23, Q24, Q25, Q26, Q27, Q28, Q29, Q30, Q31, Q32, Q33, Q34, Q35, Q36, Q37, Q38, Q39, Q40, Q41, Q42, Q43, Q44, Q45, Q46, Q47, Q48, Q49, Q50]), "depth" : 0.13 * mm});
        }
        {
            var Q0;
            Q0=makeQuery(id+"F1.opExtrude","CAP_FACE",FACE,{"disambiguationData":[OSD([sQuery(id+"F0.wireOp",EDGE,"E3"),sQuery(id+"F0.wireOp",EDGE,"E4"),sQuery(id+"F0.wireOp",EDGE,"E5"),sQuery(id+"F0.wireOp",EDGE,"E6"),sQuery(id+"F0.wireOp",EDGE,"E7"),sQuery(id+"F0.wireOp",EDGE,"E8"),sQuery(id+"F0.wireOp",EDGE,"E9"),sQuery(id+"F0.wireOp",EDGE,"E10"),sQuery(id+"F0.wireOp",EDGE,"E11"),sQuery(id+"F0.wireOp",EDGE,"E12")])],"isStart":false});
            var sketch = newSketch(context, id + "F6", { "sketchPlane" : qUnion([Q0])});
            skLineSegment(sketch, "E83.bottom", {"start": v(39.25, -45.99) * mm, "end": v(-34.41, -45.99) * mm});
            skLineSegment(sketch, "E83.top", {"start": v(39.25, 61.2) * mm, "end": v(-34.41, 61.2) * mm});
            skLineSegment(sketch, "E83.left", {"start": v(39.25, -45.99) * mm, "end": v(39.25, 61.2) * mm});
            skLineSegment(sketch, "E83.right", {"start": v(-34.41, -45.99) * mm, "end": v(-34.41, 61.2) * mm});
            skPoint(sketch, "E83.middle", {"position": v(2.42, 7.6) * mm});
            skLineSegment(sketch, "E84.0", {"start": v(31.63, 53.58) * mm, "end": v(-26.8, 53.58) * mm});
            skLineSegment(sketch, "E84.1", {"start": v(31.63, -38.37) * mm, "end": v(31.63, 53.58) * mm});
            skLineSegment(sketch, "E84.2", {"start": v(31.63, -38.37) * mm, "end": v(-26.8, -38.37) * mm});
            skLineSegment(sketch, "E84.3", {"start": v(-26.8, -38.37) * mm, "end": v(-26.8, 53.58) * mm});
            skSolve(sketch);
        }
        {
            var Q0;
            Q0=qSketchRegion(id+"F6",true);
            extrude(context, id + "F7", {"entities" : qUnion([Q0]), "operationType" : NewBodyOperationType.ADD, "oppositeDirection" : true, "depth" : 1.78 * mm});
        }
    });
